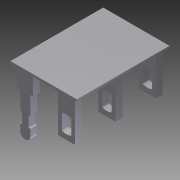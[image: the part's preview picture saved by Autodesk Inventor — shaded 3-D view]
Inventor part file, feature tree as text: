
AUTODESK INVENTOR PART (.ipt)
format: ipt  version: 2011 SP1 (Build 150282100, 282)  size: 167,936 bytes
history: native  units: in
note: dims shown in document units (in); Inventor stores cm internally (conversion verified against a paired STEP export)
features: other x7, extrude x6, sketch x6
ambient origin geometry x8: Origin, YZ Plane, XZ Plane, XY Plane, X Axis, Y Axis, Z Axis, Center Point
bodies: Solid1 (feature_tree)
feature tree (19):
  extrude  "Extrusion1"  Depth=0.401in TaperAngle=0.0deg
  extrude  "Extrusion2"  Depth=0.4in TaperAngle=0.0deg
  extrude  "Extrusion3"  Depth=0.1in TaperAngle=0.0deg
  extrude  "Extrusion4"  [1 undecoded]
  extrude  "Extrusion5"  [1 undecoded]
  extrude  "Extrusion6"  [1 undecoded]
  other  "terminal_to_body_XY"
  other  "terminal_to_body_YZ"
  other  "terminal_to_body_ZX"
  other  "terminal_to_body_X"
  other  "terminal_to_body_Y"
  other  "terminal_to_body_Z"
  other  "terminal_to_body_Center"
  sketch  "Sketch_1"  dims[d0=0.01in d1=0.0in d2=0.401in d3=0.0in]
  sketch  "Sketch_2"  dims[d4=0.401in d5=0.0in d6=0.4in d7=0.0in]
  sketch  "Sketch_3"  dims[d8=0.1in d9=0.0in d10=0.1in d11=0.0in]
  sketch  "Sketch_4"
  sketch  "Sketch_19"
  sketch  "Sketch_24"
note: 3 required parameter values undecoded (feature->parameter linkage not recoverable at this tier; creation-order binding heuristic only, values carry confidence <= 0.55)
